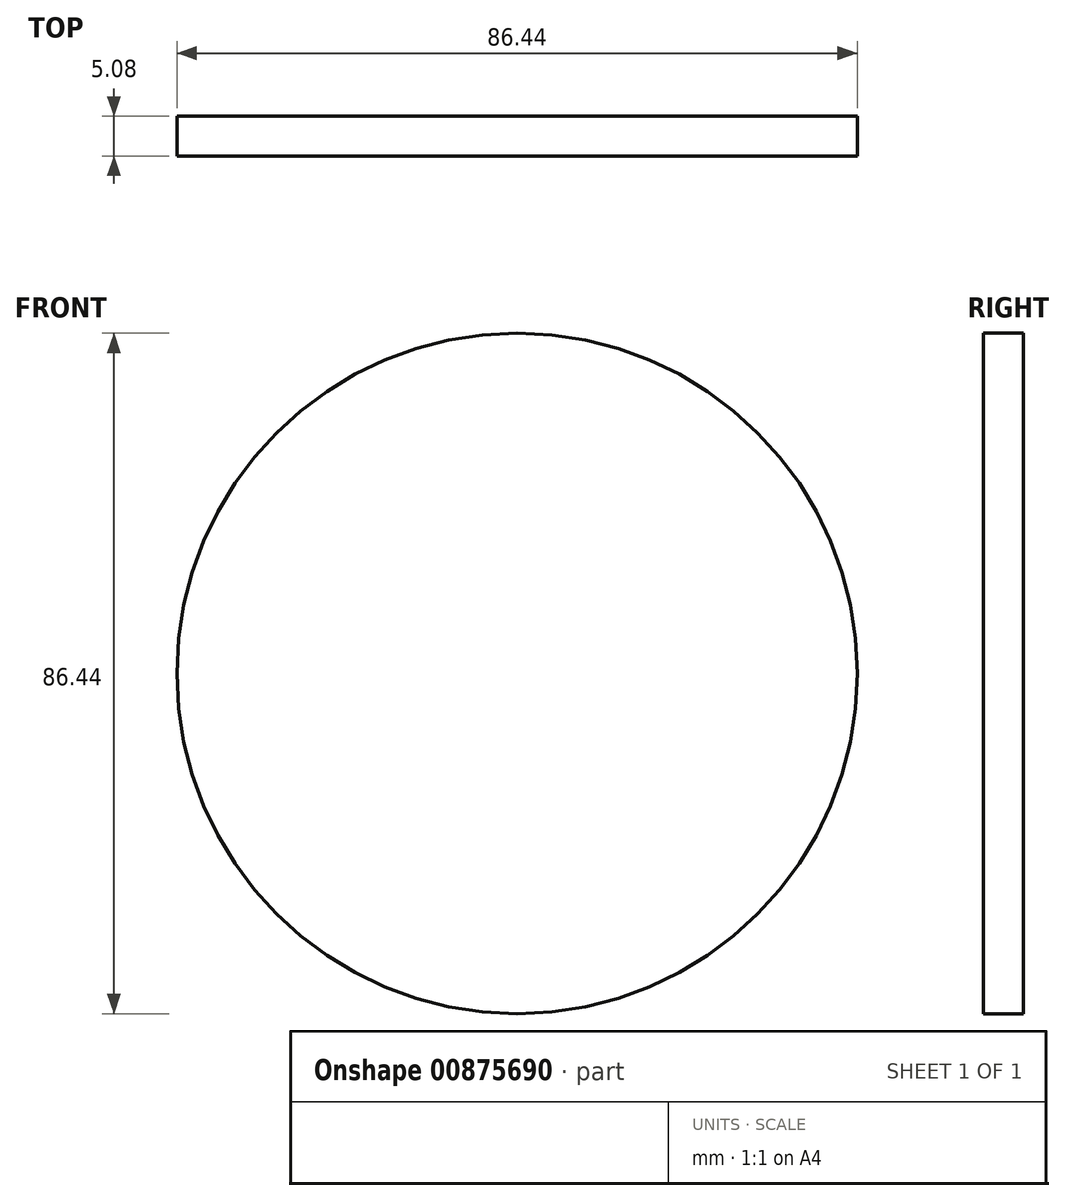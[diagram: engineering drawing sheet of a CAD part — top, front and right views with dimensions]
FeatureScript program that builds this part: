
annotation { "Feature Type Name" : "Feature", "Feature Type Description" : "" }
export const myFeature = defineFeature(function(context is Context, id is Id, definition is map)
    precondition{}
    {
        {
            var Q0;
            Q0=qCreatedBy(makeId("Front.planeOp"),FACE);
            var sketch = newSketch(context, id + "F0", { "sketchPlane" : qUnion([Q0])});
            skCircle(sketch, "E0", {"center": v(-39.75, 0) * mm, "radius": 43.22 * mm});
            skSolve(sketch);
        }
        {
            var Q0;
            Q0=makeQuery(id+"F0.imprint","IMPRINT",FACE,{"disambiguationData":[TD([[makeQuery(id+"F0.imprint","IMPRINT",EDGE,{"derivedFrom":sQuery(id+"F0.wireOp",EDGE,"E0")}),1.0]])]});
            extrude(context, id + "F1", {"entities" : qUnion([Q0]), "depth" : 5.08 * mm, "offsetDistance" : 25.4 * mm});
        }
    });
